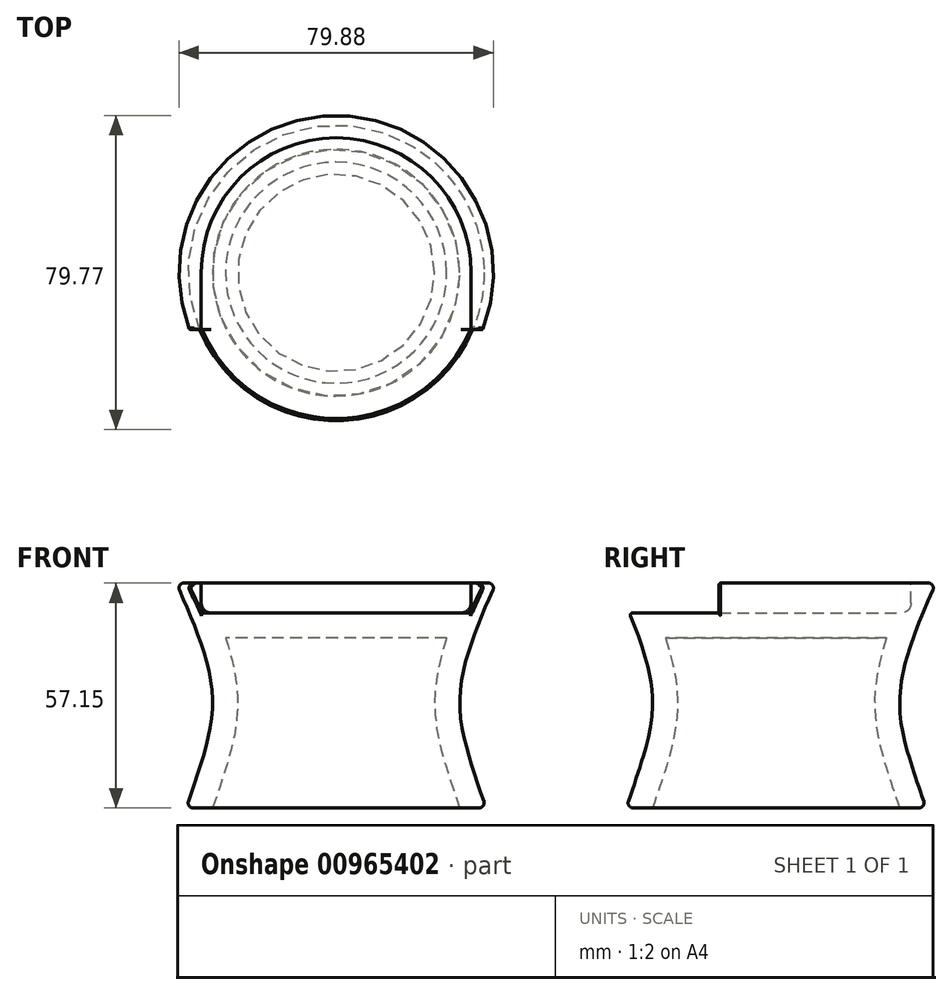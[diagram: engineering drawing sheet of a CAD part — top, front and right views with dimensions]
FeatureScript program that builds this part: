
annotation { "Feature Type Name" : "Feature", "Feature Type Description" : "" }
export const myFeature = defineFeature(function(context is Context, id is Id, definition is map)
    precondition{}
    {
        {
            var Q0;
            Q0=qCreatedBy(makeId("Front.planeOp"),FACE);
            var sketch = newSketch(context, id + "F0", { "sketchPlane" : qUnion([Q0])});
            skLineSegment(sketch, "E0", {"start": v(0, 57.15) * mm, "end": v(-40.64, 57.15) * mm});
            skLineSegment(sketch, "E1", {"start": v(0, 57.15) * mm, "end": v(0, 0) * mm});
            skLineSegment(sketch, "E2", {"start": v(0, 0) * mm, "end": v(-38.1, 0) * mm});
            skFitSpline(sketch, "E3", {"points": [v(-40.64, 57.15) * mm, v(-31.49, 29.21) * mm, v(-38.1, 0) * mm], "startDerivative": vector(30.72, -67.62) * mm, "endDerivative": vector(-29.42, -84.42) * mm});
            skSolve(sketch);
        }
        {
            var Q0;
            Q0 = qSketchRegion(id + "F0", true);
            var Q1;
            Q1=sQuery(id+"F0.wireOp",EDGE,"E1");
            revolve(context, id + "F1", {"surfaceOperationType" : NewSurfaceOperationType.NEW, "entities" : qUnion([Q0]), "axis" : qUnion([Q1]), "revolveType" : RevolveType.FULL});
        }
        {
            var Q0;
            Q0=makeQuery(id+"F1.opRevolve","SWEPT_FACE",FACE,{"disambiguationData":[OSD([sQuery(id+"F0.wireOp",EDGE,"E0")])]});
            var sketch = newSketch(context, id + "F2", { "sketchPlane" : qUnion([Q0])});
            skCircle(sketch, "E4", {"center": v(0, 0) * mm, "radius": 34.3 * mm});
            skSolve(sketch);
        }
        {
            var Q0;
            Q0 = qSketchRegion(id + "F2", true);
            extrude(context, id + "F3", {"entities" : qUnion([Q0]), "operationType" : NewBodyOperationType.REMOVE, "oppositeDirection" : true, "depth" : 7.62 * mm, "offsetDistance" : 25.4 * mm});
        }
        {
            var Q0;
            Q0=makeQuery(id+"F1.opRevolve","SWEPT_FACE",FACE,{"disambiguationData":[OSD([sQuery(id+"F0.wireOp",EDGE,"E2")])]});
            shell(context, id + "F4", {"entities" : qUnion([Q0]), "thickness" : 6.35 * mm});
        }
        {
            var Q0;
            Q0=qCreatedBy(makeId("Front.planeOp"),FACE);
            var sketch = newSketch(context, id + "F5", { "sketchPlane" : qUnion([Q0])});
            skLineSegment(sketch, "E5.bottom", {"start": v(-34.3, 57.15) * mm, "end": v(34.3, 57.15) * mm});
            skLineSegment(sketch, "E5.top", {"start": v(-34.3, 49.53) * mm, "end": v(34.3, 49.53) * mm});
            skLineSegment(sketch, "E5.left", {"start": v(-34.3, 57.15) * mm, "end": v(-34.3, 49.53) * mm});
            skLineSegment(sketch, "E5.right", {"start": v(34.3, 57.15) * mm, "end": v(34.3, 49.53) * mm});
            skSolve(sketch);
        }
        {
            var Q0;
            Q0 = qSketchRegion(id + "F5", true);
            extrude(context, id + "F6", {"entities" : qUnion([Q0]), "operationType" : NewBodyOperationType.REMOVE, "depth" : 43.18 * mm, "offsetDistance" : 25.4 * mm});
        }
        {
            var Q0;
            Q0=qCreatedBy(makeId("Right.planeOp"),FACE);
            var sketch = newSketch(context, id + "F7", { "sketchPlane" : qUnion([Q0])});
            skLineSegment(sketch, "E6.bottom", {"start": v(-14.48, 49.53) * mm, "end": v(-22.1, 49.53) * mm});
            skLineSegment(sketch, "E6.top", {"start": v(-14.48, 57.15) * mm, "end": v(-22.1, 57.15) * mm});
            skLineSegment(sketch, "E6.left", {"start": v(-14.48, 49.53) * mm, "end": v(-14.48, 57.15) * mm});
            skLineSegment(sketch, "E6.right", {"start": v(-22.1, 49.53) * mm, "end": v(-22.1, 57.15) * mm});
            skSolve(sketch);
        }
        {
            var Q0;
            Q0 = qSketchRegion(id + "F7", true);
            extrude(context, id + "F8", {"entities" : qUnion([Q0]), "operationType" : NewBodyOperationType.REMOVE, "oppositeDirection" : true, "depth" : 81.03 * mm, "offsetDistance" : 25.4 * mm, "symmetric" : true});
        }
        {
            var Q0;
            Q0=makeQuery(id+"F3.boolean.opBoolean","COPY",EDGE,{"derivedFrom":makeQuery(id+"F3.opExtrude","CAP_EDGE",EDGE,{"disambiguationData":[OSD([sQuery(id+"F2.wireOp",EDGE,"E4")])],"isStart":false})});
            fillet(context, id + "F9", {"entities" : qUnion([Q0]), "radius" : 2.54 * mm, "tangentPropagation" : true, "allowEdgeOverflow" : false});
        }
        {
            var Q0;
            Q0=makeQuery(id+"F3.boolean.opBoolean","COPY",EDGE,{"derivedFrom":makeQuery(id+"F3.opExtrude","CAP_EDGE",EDGE,{"disambiguationData":[OSD([sQuery(id+"F2.wireOp",EDGE,"E4")])],"isStart":true})});
            var Q1;
            Q1=makeQuery(id+"F1.opRevolve","SWEPT_EDGE",EDGE,{"disambiguationData":[OSD([sQuery(id+"F0.wireOp",EDGE,"E0"),sQuery(id+"F0.wireOp",EDGE,"E3")])]});
            var Q2;
            Q2=makeQuery(id+"F6.boolean.opBoolean","INTERSECT",EDGE,{"derivedFrom":[makeQuery(id+"F1.opRevolve","SWEPT_FACE",FACE,{"disambiguationData":[OSD([sQuery(id+"F0.wireOp",EDGE,"E3")])]}),makeQuery(id+"F6.opExtrude","SWEPT_FACE",FACE,{"disambiguationData":[OSD([sQuery(id+"F5.wireOp",EDGE,"E5.left")])]})]});
            var Q3;
            Q3=makeQuery(id+"F1.opRevolve","SWEPT_EDGE",EDGE,{"disambiguationData":[OSD([sQuery(id+"F0.wireOp",EDGE,"E2"),sQuery(id+"F0.wireOp",EDGE,"E3")])]});
            fillet(context, id + "F10", {"entities" : qUnion([Q0, Q1, Q2, Q3]), "radius" : 1.27 * mm, "tangentPropagation" : true, "allowEdgeOverflow" : false});
        }
        {
            var Q0;
            Q0=makeQuery(id+"F8.boolean.opBoolean","INTERSECT",EDGE,{"disambiguationData":[OD(0.0)],"derivedFrom":[makeQuery(id+"F1.opRevolve","SWEPT_FACE",FACE,{"disambiguationData":[OSD([sQuery(id+"F0.wireOp",EDGE,"E3")])]}),makeQuery(id+"F8.opExtrude","SWEPT_FACE",FACE,{"disambiguationData":[OSD([sQuery(id+"F7.wireOp",EDGE,"E6.left")])]})]});
            fillet(context, id + "F11", {"entities" : qUnion([Q0]), "radius" : 0.5 * mm, "tangentPropagation" : true, "allowEdgeOverflow" : false});
        }
        {
            var Q0;
            Q0=makeQuery(id+"F8.boolean.opBoolean","INTERSECT",EDGE,{"derivedFrom":[makeQuery(id+"F1.opRevolve","SWEPT_FACE",FACE,{"disambiguationData":[OSD([sQuery(id+"F0.wireOp",EDGE,"E3")])]}),makeQuery(id+"F8.opExtrude","SWEPT_FACE",FACE,{"disambiguationData":[OSD([sQuery(id+"F7.wireOp",EDGE,"E6.bottom")])]})]});
            fillet(context, id + "F12", {"entities" : qUnion([Q0]), "radius" : 0.5 * mm, "tangentPropagation" : true, "allowEdgeOverflow" : false});
        }
        {
            var Q0;
            Q0=makeQuery(id+"F8.boolean.opBoolean","INTERSECT",EDGE,{"disambiguationData":[OD(1.0)],"derivedFrom":[makeQuery(id+"F1.opRevolve","SWEPT_FACE",FACE,{"disambiguationData":[OSD([sQuery(id+"F0.wireOp",EDGE,"E3")])]}),makeQuery(id+"F8.opExtrude","SWEPT_FACE",FACE,{"disambiguationData":[OSD([sQuery(id+"F7.wireOp",EDGE,"E6.left")])]})]});
            fillet(context, id + "F13", {"entities" : qUnion([Q0]), "radius" : 0.5 * mm, "tangentPropagation" : true, "allowEdgeOverflow" : false});
        }
    });
